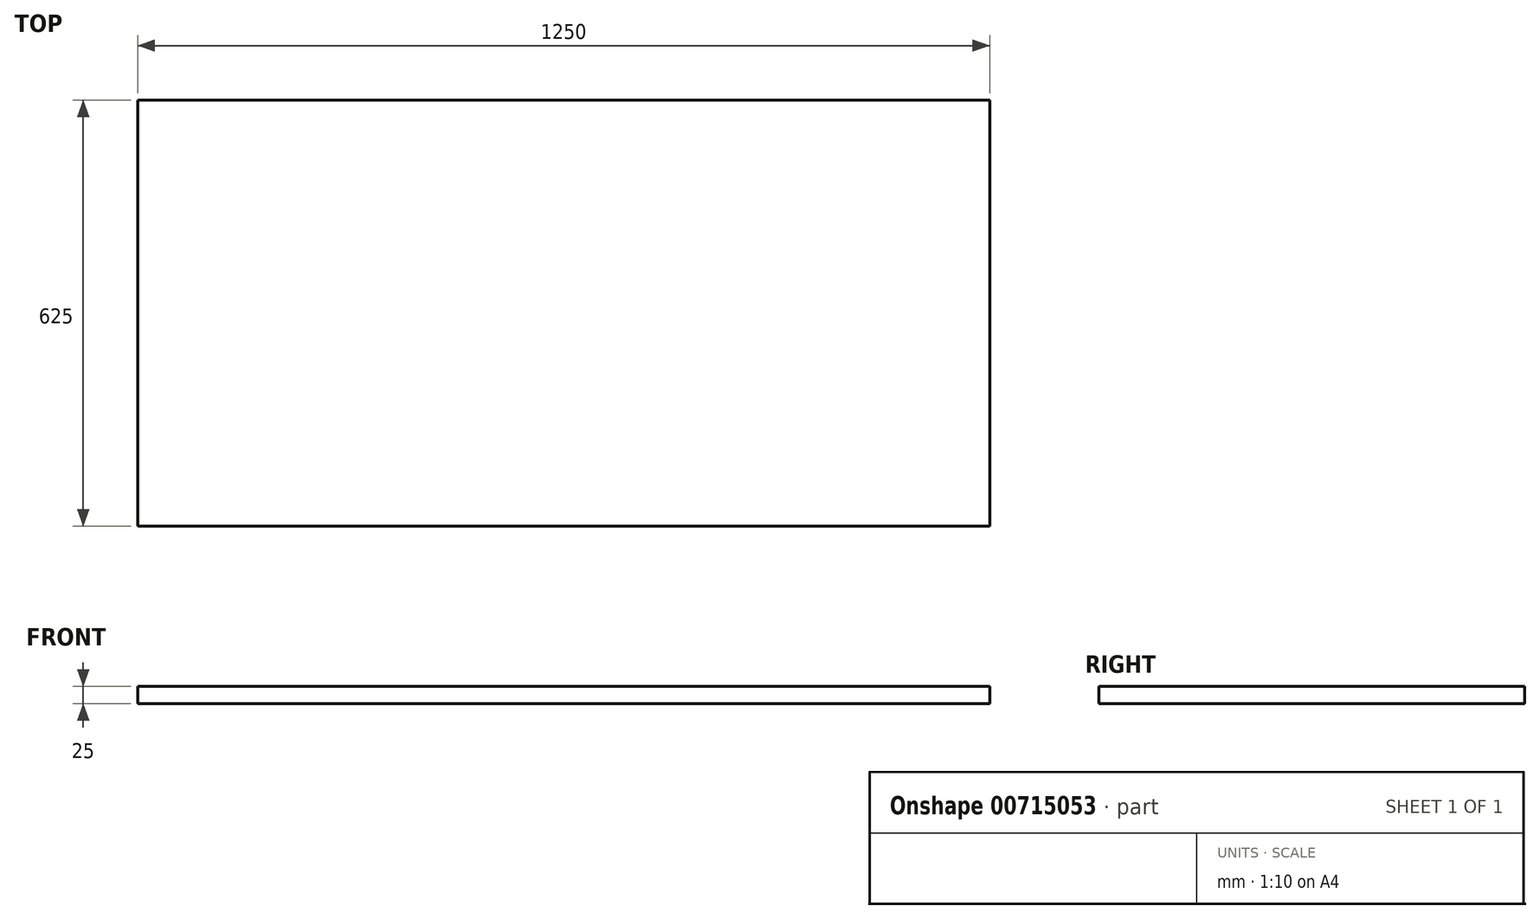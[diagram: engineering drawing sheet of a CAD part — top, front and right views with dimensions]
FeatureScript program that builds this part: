
annotation { "Feature Type Name" : "Feature", "Feature Type Description" : "" }
export const myFeature = defineFeature(function(context is Context, id is Id, definition is map)
    precondition{}
    {
        {
            var Q0;
            Q0=qCreatedBy(makeId("Top.planeOp"),FACE);
            var sketch = newSketch(context, id + "F0", { "sketchPlane" : qUnion([Q0])});
            skLineSegment(sketch, "E0.bottom", {"start": v(625, 312.5) * mm, "end": v(-625, 312.5) * mm});
            skLineSegment(sketch, "E0.top", {"start": v(625, -312.5) * mm, "end": v(-625, -312.5) * mm});
            skLineSegment(sketch, "E0.left", {"start": v(625, 312.5) * mm, "end": v(625, -312.5) * mm});
            skLineSegment(sketch, "E0.right", {"start": v(-625, 312.5) * mm, "end": v(-625, -312.5) * mm});
            skPoint(sketch, "E0.middle", {"position": v(0, 0) * mm});
            skSolve(sketch);
        }
        {
            var Q0;
            Q0=makeQuery(id+"F0.imprint","IMPRINT",FACE,{"disambiguationData":[TD([[makeQuery(id+"F0.imprint","IMPRINT",EDGE,{"derivedFrom":sQuery(id+"F0.wireOp",EDGE,"E0.bottom")}),1.0]])]});
            extrude(context, id + "F1", {"entities" : qUnion([Q0]), "depth" : 25 * mm, "offsetDistance" : 25 * mm});
        }
    });
